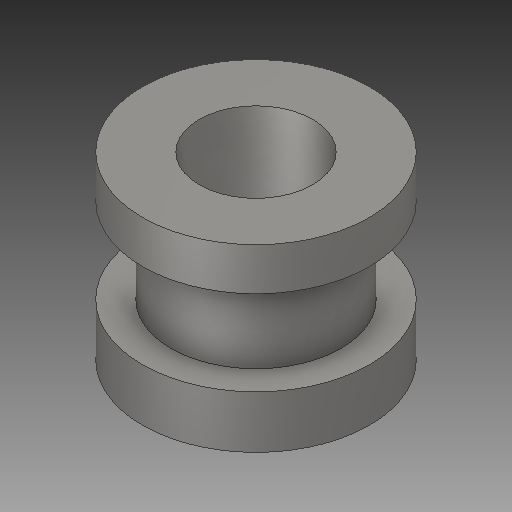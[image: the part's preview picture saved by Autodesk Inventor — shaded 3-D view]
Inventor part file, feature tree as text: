
AUTODESK INVENTOR PART (.ipt)
format: ipt  version: 2019 (Build 230136000, 136)  size: 150,016 bytes
history: native  units: mm
features: revolve x1, sketch x1
ambient origin geometry x8: Origin, YZ Plane, XZ Plane, XY Plane, X Axis, Y Axis, Z Axis, Center Point
bodies: Body1 (feature_tree)
feature tree (2):
  revolve  "Revolution2"  [1 undecoded]
  sketch  "Sketch1"  dims[d1=8.0mm d2=3.7mm d3=3.0mm d4=6.0mm d5=6.0mm d7=4.0mm d8=2.1mm d9=7.0mm d11=4.0mm d12=90.0deg]
note: 1 required parameter value undecoded (feature->parameter linkage not recoverable at this tier; creation-order binding heuristic only, values carry confidence <= 0.55)
